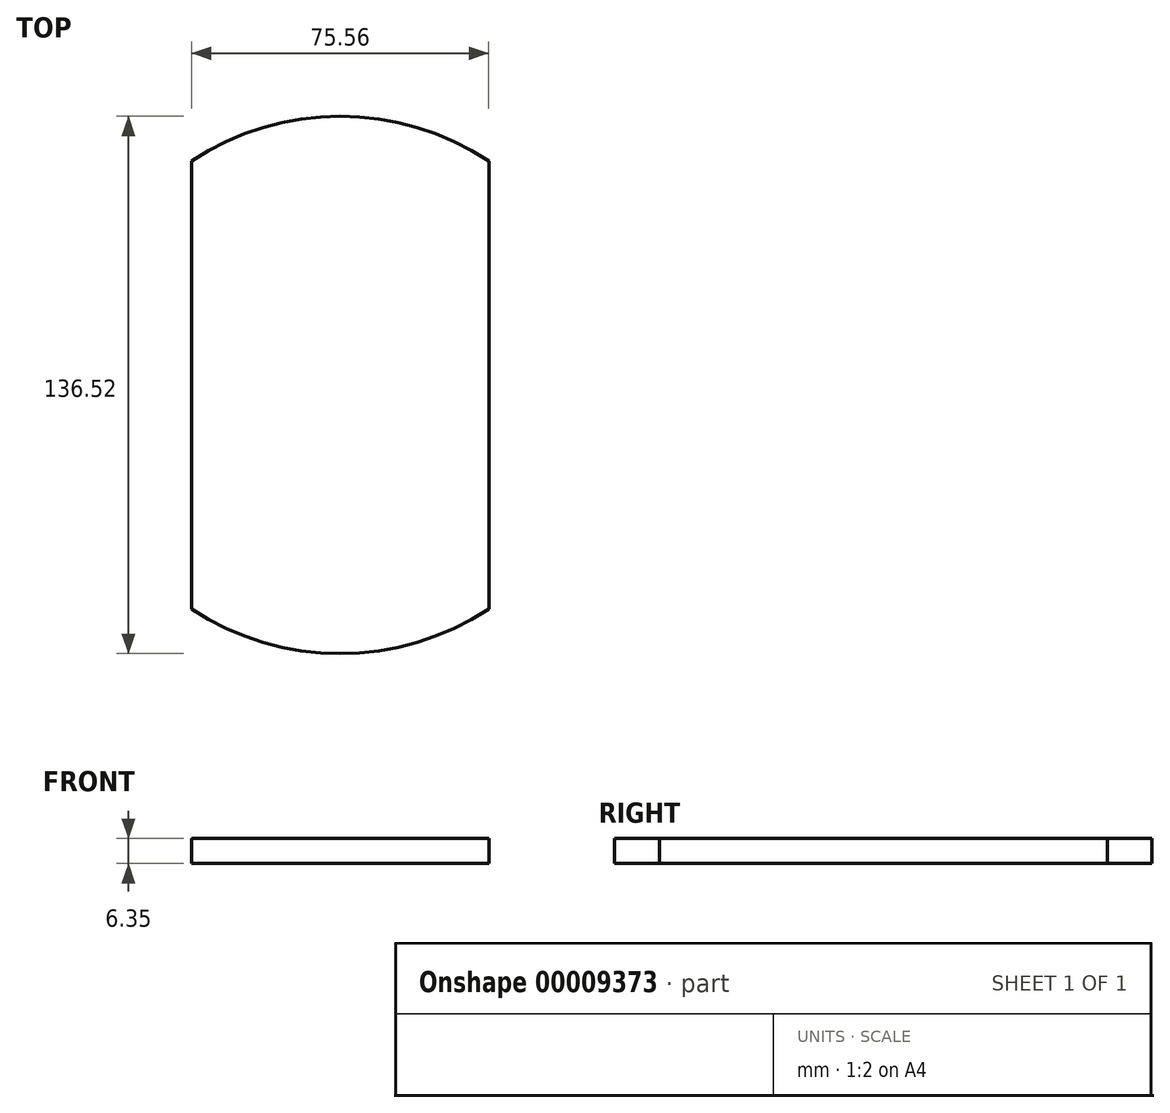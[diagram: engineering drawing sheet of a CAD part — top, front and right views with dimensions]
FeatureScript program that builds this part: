
annotation { "Feature Type Name" : "Feature", "Feature Type Description" : "" }
export const myFeature = defineFeature(function(context is Context, id is Id, definition is map)
    precondition{}
    {
        {
            var Q0;
            Q0=qCreatedBy(makeId("Top.planeOp"),FACE);
            var sketch = newSketch(context, id + "F0", { "sketchPlane" : qUnion([Q0])});
            skCircle(sketch, "E0", {"center": v(0, 0) * mm, "radius": 68.26 * mm});
            skLineSegment(sketch, "E1.rect.bottom", {"start": v(37.78, 56.85) * mm, "end": v(-37.78, 56.85) * mm});
            skLineSegment(sketch, "E1.rect.top", {"start": v(37.78, -56.85) * mm, "end": v(-37.78, -56.85) * mm});
            skLineSegment(sketch, "E1.rect.left", {"start": v(37.78, 56.85) * mm, "end": v(37.78, -56.85) * mm});
            skLineSegment(sketch, "E1.rect.right", {"start": v(-37.78, 56.85) * mm, "end": v(-37.78, -56.85) * mm});
            skSolve(sketch);
        }
        {
            var Q0;
            {var subQ0=sQuery(id+"F0.wireOp",EDGE,"E1.rect.bottom");Q0=makeQuery(id+"F0.imprint","IMPRINT",FACE,{"disambiguationData":[TD([[makeQuery(id+"F0.imprint","IMPRINT",EDGE,{"derivedFrom":subQ0}),-1.0]])]});}
            var Q1;
            Q1=makeQuery(id+"F0.imprint","IMPRINT",FACE,{"disambiguationData":[TD([[makeQuery(id+"F0.imprint","IMPRINT",EDGE,{"derivedFrom":sQuery(id+"F0.wireOp",EDGE,"E1.rect.bottom")}),1.0]])]});
            var Q2;
            {var subQ0=sQuery(id+"F0.wireOp",EDGE,"E1.rect.top");Q2=makeQuery(id+"F0.imprint","IMPRINT",FACE,{"disambiguationData":[TD([[makeQuery(id+"F0.imprint","IMPRINT",EDGE,{"derivedFrom":subQ0}),1.0]])]});}
            extrude(context, id + "F1", {"entities" : qUnion([Q0, Q1, Q2]), "depth" : 6.35 * mm});
        }
    });
